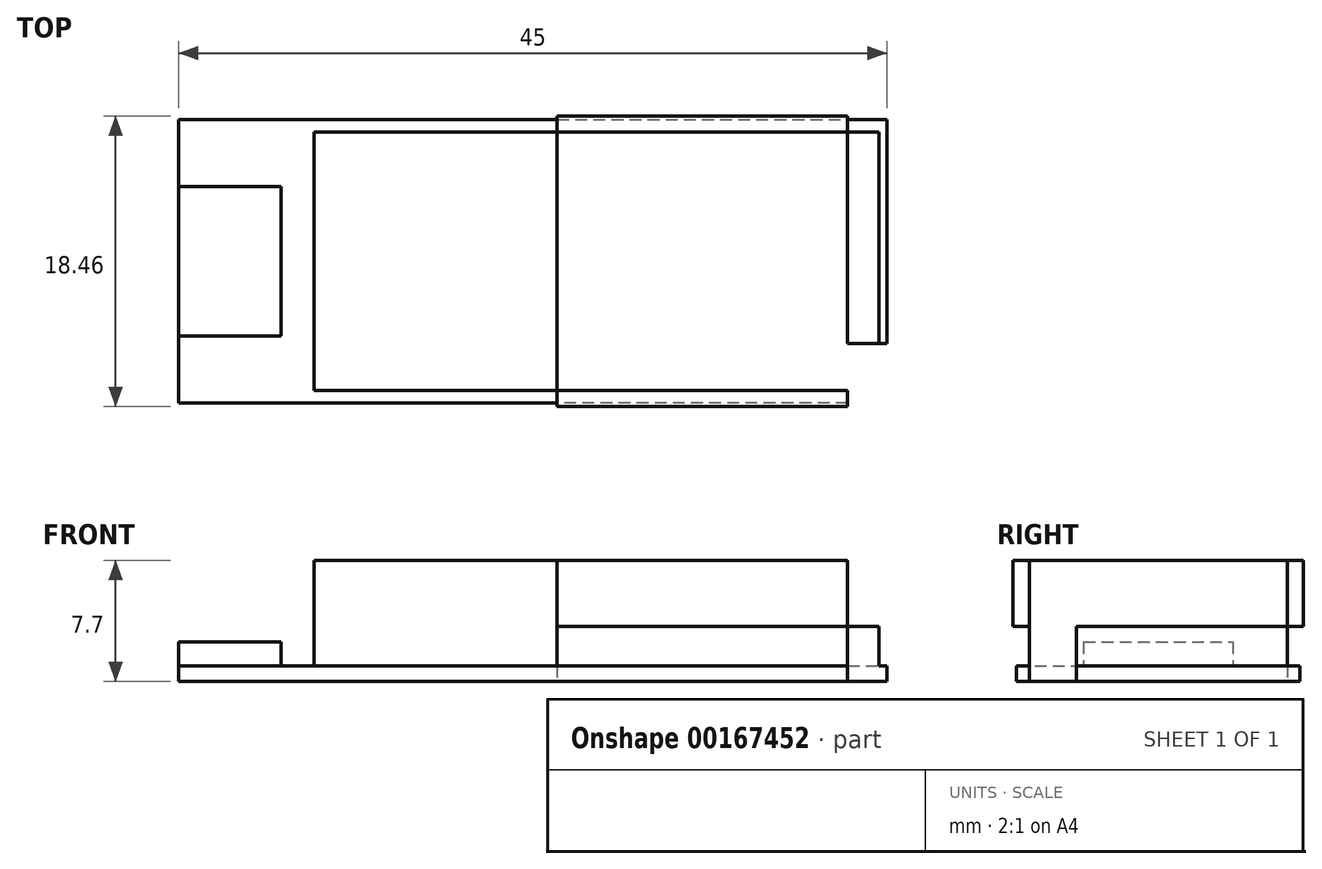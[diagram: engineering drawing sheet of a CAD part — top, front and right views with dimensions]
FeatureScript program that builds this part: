
annotation { "Feature Type Name" : "Feature", "Feature Type Description" : "" }
export const myFeature = defineFeature(function(context is Context, id is Id, definition is map)
    precondition{}
    {
        {
            var Q0;
            Q0=qCreatedBy(makeId("Top.planeOp"),FACE);
            var sketch = newSketch(context, id + "F0", { "sketchPlane" : qUnion([Q0])});
            skLineSegment(sketch, "E0", {"start": v(0, 0) * mm, "end": v(45, 0) * mm});
            skLineSegment(sketch, "E1", {"start": v(45, 0) * mm, "end": v(45, -14.2) * mm});
            skLineSegment(sketch, "E2", {"start": v(45, -14.2) * mm, "end": v(42.5, -14.2) * mm});
            skLineSegment(sketch, "E3", {"start": v(42.5, -14.2) * mm, "end": v(42.5, -18) * mm});
            skLineSegment(sketch, "E4", {"start": v(42.5, -18) * mm, "end": v(0, -18) * mm});
            skLineSegment(sketch, "E5", {"start": v(0, -18) * mm, "end": v(0, 0) * mm});
            skLineSegment(sketch, "E6", {"start": v(8.6, -0.8) * mm, "end": v(8.6, -17.2) * mm});
            skLineSegment(sketch, "E7", {"start": v(42.5, -17.2) * mm, "end": v(8.6, -17.2) * mm});
            skLineSegment(sketch, "E8", {"start": v(44.5, -14.2) * mm, "end": v(44.5, -0.8) * mm});
            skLineSegment(sketch, "E9", {"start": v(44.5, -0.8) * mm, "end": v(8.6, -0.8) * mm});
            skLineSegment(sketch, "E10.bottom", {"start": v(24.05, 0.23) * mm, "end": v(42.5, 0.23) * mm});
            skLineSegment(sketch, "E10.top", {"start": v(24.05, -18.23) * mm, "end": v(42.5, -18.23) * mm});
            skLineSegment(sketch, "E10.left", {"start": v(24.05, 0.22) * mm, "end": v(24.05, -18.23) * mm});
            skLineSegment(sketch, "E10.right", {"start": v(42.5, 0.22) * mm, "end": v(42.5, -18.23) * mm});
            skLineSegment(sketch, "E11", {"start": v(0, -4.25) * mm, "end": v(6.5, -4.25) * mm});
            skLineSegment(sketch, "E12", {"start": v(6.5, -4.25) * mm, "end": v(6.5, -13.75) * mm});
            skLineSegment(sketch, "E13", {"start": v(6.5, -13.75) * mm, "end": v(0, -13.75) * mm});
            skPoint(sketch, "E14", {"position": v(45, -9) * mm});
            skSolve(sketch);
        }
        {
            var Q0;
            {var subQ1=sQuery(id+"F0.wireOp",EDGE,"E11");Q0=makeQuery(id+"F0.imprint","IMPRINT",FACE,{"disambiguationData":[TD([[makeQuery(id+"F0.imprint","IMPRINT",EDGE,{"derivedFrom":subQ1}),-1.0]])]});}
            var Q1;
            {var subQ5=sQuery(id+"F0.wireOp",EDGE,"E8");Q1=makeQuery(id+"F0.imprint","IMPRINT",FACE,{"disambiguationData":[TD([[makeQuery(id+"F0.imprint","IMPRINT",EDGE,{"derivedFrom":subQ5}),1.0]])]});}
            var Q2;
            {var subQ7=sQuery(id+"F0.wireOp",EDGE,"E1");Q2=makeQuery(id+"F0.imprint","IMPRINT",FACE,{"disambiguationData":[TD([[makeQuery(id+"F0.imprint","IMPRINT",EDGE,{"derivedFrom":subQ7}),-1.0]])]});}
            var Q3;
            {var subQ5=sQuery(id+"F0.wireOp",EDGE,"E6");Q3=makeQuery(id+"F0.imprint","IMPRINT",FACE,{"disambiguationData":[TD([[makeQuery(id+"F0.imprint","IMPRINT",EDGE,{"derivedFrom":subQ5}),1.0]])]});}
            var Q4;
            {var subQ0=sQuery(id+"F0.wireOp",EDGE,"E10.right");var subQ1=sQuery(id+"F0.wireOp",EDGE,"E7");var subQ2=makeQuery(id+"F0.imprint","INTERSECT",VERTEX,{"derivedFrom":[subQ1,subQ0]});Q4=makeQuery(id+"F0.imprint","IMPRINT",FACE,{"disambiguationData":[TD([[makeQuery(id+"F0.imprint","IMPRINT",EDGE,{"disambiguationData":[TD([[subQ2,-1.0]])],"derivedFrom":subQ1}),-1.0]])]});}
            var Q5;
            {var subQ3=sQuery(id+"F0.wireOp",EDGE,"E0");var subQ5=sQuery(id+"F0.wireOp",EDGE,"E10.left");var subQ7=makeQuery(id+"F0.imprint","INTERSECT",VERTEX,{"derivedFrom":[subQ3,subQ5]});Q5=makeQuery(id+"F0.imprint","IMPRINT",FACE,{"disambiguationData":[TD([[makeQuery(id+"F0.imprint","IMPRINT",EDGE,{"disambiguationData":[TD([[subQ7,-1.0]])],"derivedFrom":subQ3}),-1.0]])]});}
            var Q6;
            {var subQ11=sQuery(id+"F0.wireOp",EDGE,"E6");Q6=makeQuery(id+"F0.imprint","IMPRINT",FACE,{"disambiguationData":[TD([[makeQuery(id+"F0.imprint","IMPRINT",EDGE,{"derivedFrom":subQ11}),-1.0]])]});}
            var Q7;
            {var subQ0=sQuery(id+"F0.wireOp",EDGE,"E10.right");var subQ3=sQuery(id+"F0.wireOp",EDGE,"E4");var subQ4=makeQuery(id+"F0.imprint","INTERSECT",VERTEX,{"derivedFrom":[subQ3,subQ0]});Q7=makeQuery(id+"F0.imprint","IMPRINT",FACE,{"disambiguationData":[TD([[makeQuery(id+"F0.imprint","IMPRINT",EDGE,{"disambiguationData":[TD([[subQ4,-1.0]])],"derivedFrom":subQ3}),-1.0]])]});}
            extrude(context, id + "F1", {"entities" : qUnion([Q0, Q1, Q2, Q3, Q4, Q5, Q6, Q7]), "depth" : 1 * mm});
        }
        {
            var Q0;
            {var subQ5=sQuery(id+"F0.wireOp",EDGE,"E6");Q0=makeQuery(id+"F0.imprint","IMPRINT",FACE,{"disambiguationData":[TD([[makeQuery(id+"F0.imprint","IMPRINT",EDGE,{"derivedFrom":subQ5}),1.0]])]});}
            var Q1;
            {var subQ0=sQuery(id+"F0.wireOp",EDGE,"E10.right");var subQ1=sQuery(id+"F0.wireOp",EDGE,"E7");var subQ2=makeQuery(id+"F0.imprint","INTERSECT",VERTEX,{"derivedFrom":[subQ1,subQ0]});Q1=makeQuery(id+"F0.imprint","IMPRINT",FACE,{"disambiguationData":[TD([[makeQuery(id+"F0.imprint","IMPRINT",EDGE,{"disambiguationData":[TD([[subQ2,-1.0]])],"derivedFrom":subQ1}),-1.0]])]});}
            var Q2;
            {var subQ5=sQuery(id+"F0.wireOp",EDGE,"E8");Q2=makeQuery(id+"F0.imprint","IMPRINT",FACE,{"disambiguationData":[TD([[makeQuery(id+"F0.imprint","IMPRINT",EDGE,{"derivedFrom":subQ5}),1.0]])]});}
            extrude(context, id + "F2", {"entities" : qUnion([Q0, Q1, Q2]), "operationType" : NewBodyOperationType.ADD, "depth" : 3.5 * mm});
        }
        {
            var Q0;
            {var subQ3=sQuery(id+"F0.wireOp",EDGE,"E0");var subQ5=sQuery(id+"F0.wireOp",EDGE,"E10.left");var subQ7=makeQuery(id+"F0.imprint","INTERSECT",VERTEX,{"derivedFrom":[subQ3,subQ5]});Q0=makeQuery(id+"F0.imprint","IMPRINT",FACE,{"disambiguationData":[TD([[makeQuery(id+"F0.imprint","IMPRINT",EDGE,{"disambiguationData":[TD([[subQ7,-1.0]])],"derivedFrom":subQ3}),-1.0]])]});}
            var Q1;
            {var subQ3=sQuery(id+"F0.wireOp",EDGE,"E10.bottom");Q1=makeQuery(id+"F0.imprint","IMPRINT",FACE,{"disambiguationData":[TD([[makeQuery(id+"F0.imprint","IMPRINT",EDGE,{"derivedFrom":subQ3}),-1.0]])]});}
            var Q2;
            {var subQ0=sQuery(id+"F0.wireOp",EDGE,"E10.right");var subQ1=sQuery(id+"F0.wireOp",EDGE,"E7");var subQ2=makeQuery(id+"F0.imprint","INTERSECT",VERTEX,{"derivedFrom":[subQ1,subQ0]});Q2=makeQuery(id+"F0.imprint","IMPRINT",FACE,{"disambiguationData":[TD([[makeQuery(id+"F0.imprint","IMPRINT",EDGE,{"disambiguationData":[TD([[subQ2,-1.0]])],"derivedFrom":subQ1}),-1.0]])]});}
            var Q3;
            {var subQ0=sQuery(id+"F0.wireOp",EDGE,"E10.right");var subQ3=sQuery(id+"F0.wireOp",EDGE,"E4");var subQ4=makeQuery(id+"F0.imprint","INTERSECT",VERTEX,{"derivedFrom":[subQ3,subQ0]});Q3=makeQuery(id+"F0.imprint","IMPRINT",FACE,{"disambiguationData":[TD([[makeQuery(id+"F0.imprint","IMPRINT",EDGE,{"disambiguationData":[TD([[subQ4,-1.0]])],"derivedFrom":subQ3}),-1.0]])]});}
            var Q4;
            {var subQ1=sQuery(id+"F0.wireOp",EDGE,"E10.top");Q4=makeQuery(id+"F0.imprint","IMPRINT",FACE,{"disambiguationData":[TD([[makeQuery(id+"F0.imprint","IMPRINT",EDGE,{"derivedFrom":subQ1}),1.0]])]});}
            extrude(context, id + "F3", {"entities" : qUnion([Q0, Q1, Q2, Q3, Q4]), "operationType" : NewBodyOperationType.ADD, "depth" : 7.7 * mm, "hasSecondDirection" : true, "secondDirectionOppositeDirection" : false, "secondDirectionDepth" : 3.5 * mm});
        }
        {
            var Q0;
            {var subQ1=sQuery(id+"F0.wireOp",EDGE,"E11");Q0=makeQuery(id+"F0.imprint","IMPRINT",FACE,{"disambiguationData":[TD([[makeQuery(id+"F0.imprint","IMPRINT",EDGE,{"derivedFrom":subQ1}),-1.0]])]});}
            extrude(context, id + "F4", {"entities" : qUnion([Q0]), "operationType" : NewBodyOperationType.ADD, "depth" : 2.5 * mm});
        }
    });
